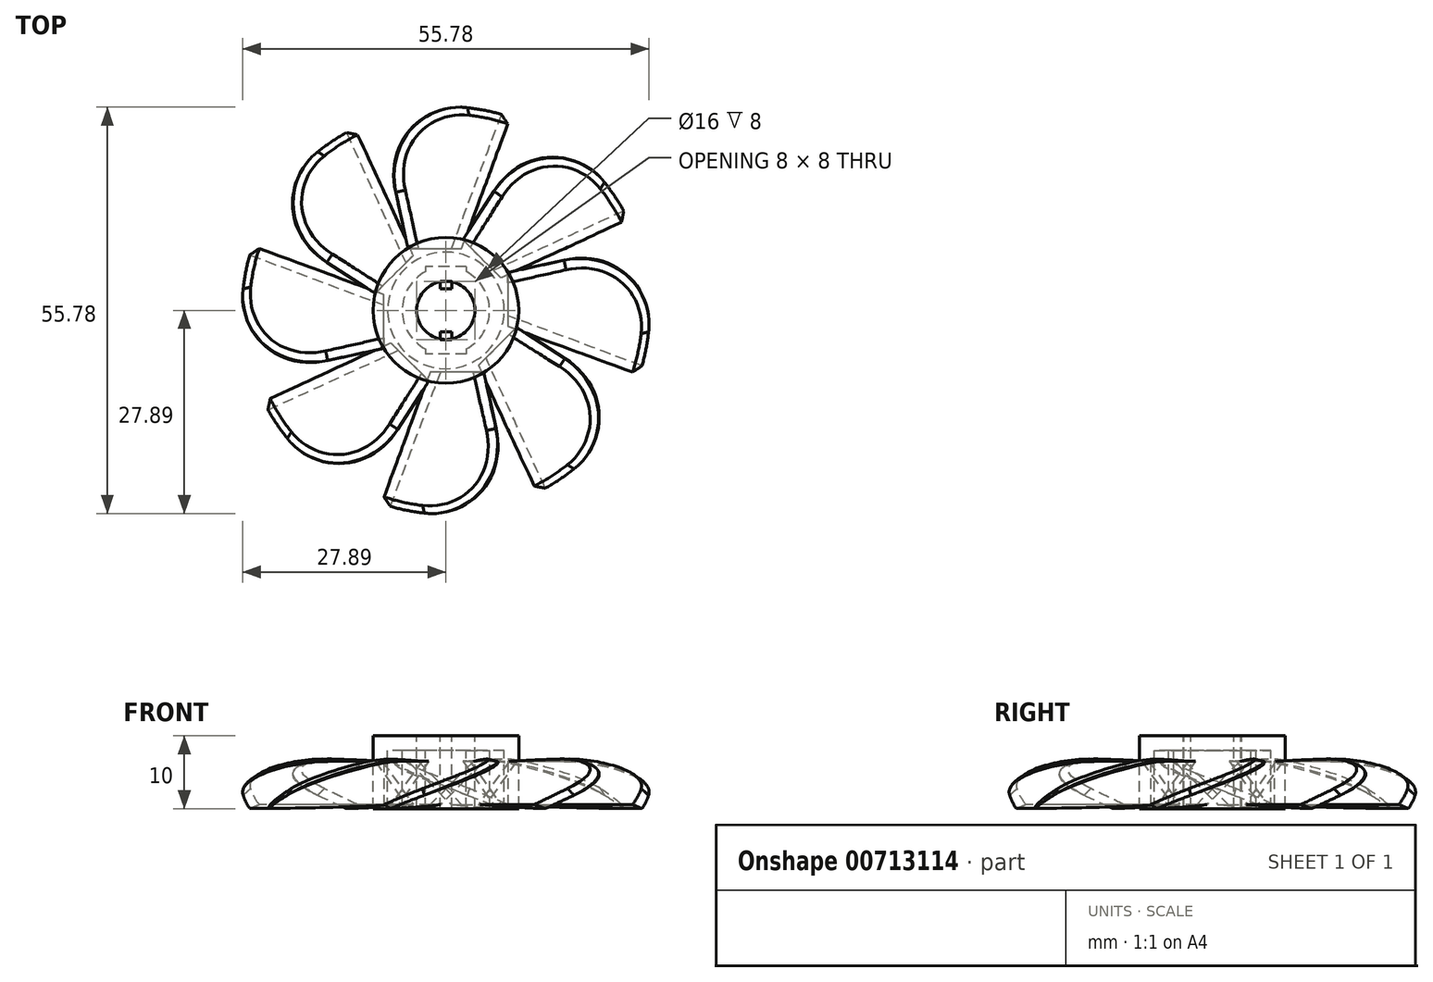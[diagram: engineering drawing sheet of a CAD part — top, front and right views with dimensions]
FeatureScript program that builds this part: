
annotation { "Feature Type Name" : "Feature", "Feature Type Description" : "" }
export const myFeature = defineFeature(function(context is Context, id is Id, definition is map)
    precondition{}
    {
        {
            var Q0;
            Q0=qCreatedBy(makeId("Top.planeOp"),FACE);
            var sketch = newSketch(context, id + "F0", { "sketchPlane" : qUnion([Q0])});
            skCircle(sketch, "E0", {"center": v(0, 0) * mm, "radius": 4 * mm});
            skCircle(sketch, "E1", {"center": v(0, 0) * mm, "radius": 10 * mm});
            skLineSegment(sketch, "E2.bottom", {"start": v(0.8, 4) * mm, "end": v(-0.8, 4) * mm});
            skLineSegment(sketch, "E2.top", {"start": v(0.8, -4) * mm, "end": v(-0.8, -4) * mm});
            skLineSegment(sketch, "E2.left", {"start": v(0.8, 4) * mm, "end": v(0.8, -4) * mm});
            skLineSegment(sketch, "E2.right", {"start": v(-0.8, 4) * mm, "end": v(-0.8, -4) * mm});
            skCircle(sketch, "E3", {"center": v(0, 0) * mm, "radius": 28 * mm});
            skCircle(sketch, "E4", {"center": v(0, 0) * mm, "radius": 44.62 * mm});
            skLineSegment(sketch, "E5.bottom", {"start": v(-0.8, 4) * mm, "end": v(0.8, 4) * mm});
            skLineSegment(sketch, "E5.top", {"start": v(-0.8, 2.95) * mm, "end": v(0.8, 2.95) * mm});
            skLineSegment(sketch, "E5.left", {"start": v(-0.8, 4) * mm, "end": v(-0.8, 2.95) * mm});
            skLineSegment(sketch, "E5.right", {"start": v(0.8, 4) * mm, "end": v(0.8, 2.95) * mm});
            skLineSegment(sketch, "E6.bottom", {"start": v(-0.8, -4) * mm, "end": v(0.8, -4) * mm});
            skLineSegment(sketch, "E6.top", {"start": v(-0.8, -2.95) * mm, "end": v(0.8, -2.95) * mm});
            skLineSegment(sketch, "E6.left", {"start": v(-0.8, -4) * mm, "end": v(-0.8, -2.95) * mm});
            skLineSegment(sketch, "E6.right", {"start": v(0.8, -4) * mm, "end": v(0.8, -2.95) * mm});
            skSolve(sketch);
        }
        {
            var Q0;
            Q0=makeQuery(id+"F0.imprint","IMPRINT",FACE,{"disambiguationData":[TD([[makeQuery(id+"F0.imprint","IMPRINT",EDGE,{"derivedFrom":sQuery(id+"F0.wireOp",EDGE,"E1")}),1.0]])]});
            var Q1;
            {var subQ0=sQuery(id+"F0.wireOp",EDGE,"E5.top");Q1=makeQuery(id+"F0.imprint","IMPRINT",FACE,{"disambiguationData":[TD([[makeQuery(id+"F0.imprint","IMPRINT",EDGE,{"derivedFrom":subQ0}),1.0]])]});}
            var Q2;
            {var subQ1=sQuery(id+"F0.wireOp",EDGE,"E6.top");Q2=makeQuery(id+"F0.imprint","IMPRINT",FACE,{"disambiguationData":[TD([[makeQuery(id+"F0.imprint","IMPRINT",EDGE,{"derivedFrom":subQ1}),-1.0]])]});}
            var Q3;
            {var subQ0=sQuery(id+"F0.wireOp",EDGE,"E6.bottom");var subQ1=sQuery(id+"F0.wireOp",EDGE,"E0");var subQ2=makeQuery(id+"F0.imprint","INTERSECT",VERTEX,{"derivedFrom":[subQ1,subQ0]});Q3=makeQuery(id+"F0.imprint","IMPRINT",FACE,{"disambiguationData":[TD([[makeQuery(id+"F0.imprint","IMPRINT",EDGE,{"disambiguationData":[TD([[subQ2,-1.0]])],"derivedFrom":subQ1}),-1.0]])]});}
            var Q4;
            {var subQ0=sQuery(id+"F0.wireOp",EDGE,"E6.left");var subQ1=sQuery(id+"F0.wireOp",EDGE,"E0");var subQ2=makeQuery(id+"F0.imprint","INTERSECT",VERTEX,{"derivedFrom":[subQ1,subQ0]});Q4=makeQuery(id+"F0.imprint","IMPRINT",FACE,{"disambiguationData":[TD([[makeQuery(id+"F0.imprint","IMPRINT",EDGE,{"disambiguationData":[TD([[subQ2,-1.0]])],"derivedFrom":subQ1}),-1.0]])]});}
            var Q5;
            {var subQ0=sQuery(id+"F0.wireOp",EDGE,"E5.bottom");var subQ1=sQuery(id+"F0.wireOp",EDGE,"E0");var subQ2=makeQuery(id+"F0.imprint","INTERSECT",VERTEX,{"derivedFrom":[subQ1,subQ0]});Q5=makeQuery(id+"F0.imprint","IMPRINT",FACE,{"disambiguationData":[TD([[makeQuery(id+"F0.imprint","IMPRINT",EDGE,{"disambiguationData":[TD([[subQ2,-1.0]])],"derivedFrom":subQ1}),-1.0]])]});}
            var Q6;
            {var subQ0=sQuery(id+"F0.wireOp",EDGE,"E5.bottom");var subQ1=sQuery(id+"F0.wireOp",EDGE,"E0");var subQ2=makeQuery(id+"F0.imprint","INTERSECT",VERTEX,{"derivedFrom":[subQ1,subQ0]});Q6=makeQuery(id+"F0.imprint","IMPRINT",FACE,{"disambiguationData":[TD([[makeQuery(id+"F0.imprint","IMPRINT",EDGE,{"disambiguationData":[TD([[subQ2,1.0]])],"derivedFrom":subQ1}),-1.0]])]});}
            extrude(context, id + "F1", {"entities" : qUnion([Q0, Q1, Q2, Q3, Q4, Q5, Q6]), "oppositeDirection" : true, "depth" : 10 * mm, "offsetDistance" : 25 * mm});
        }
        {
            var Q0;
            Q0=makeQuery(id+"F1.opExtrude","CAP_FACE",FACE,{"disambiguationData":[OSD([sQuery(id+"F0.wireOp",EDGE,"E1")])],"isStart":false});
            shell(context, id + "F2", {"entities" : qUnion([Q0]), "thickness" : 2 * mm});
        }
        {
            var Q0;
            Q0=qCreatedBy(makeId("Right.planeOp"),FACE);
            var sketch = newSketch(context, id + "F3", { "sketchPlane" : qUnion([Q0])});
            skLineSegment(sketch, "E7", {"start": v(0, 0) * mm, "end": v(0, -13) * mm});
            skSolve(sketch);
        }
        {
            var Q0;
            Q0=qCreatedBy(makeId("Front.planeOp"),FACE);
            cPlane(context, id + "F4", {"entities" : qUnion([Q0]), "cplaneType" : CPlaneType.OFFSET, "offset" : 8.5 * mm, "width" : 150 * mm, "height" : 150 * mm});
        }
        {
            var Q0;
            Q0=qCreatedBy(id+"F4.planeOp",FACE);
            var sketch = newSketch(context, id + "F5", { "sketchPlane" : qUnion([Q0])});
            skLineSegment(sketch, "E8", {"start": v(0, 0) * mm, "end": v(0, -6.5) * mm});
            skLineSegment(sketch, "E9.bottom", {"start": v(5.21, -3.5) * mm, "end": v(4.5, -2.79) * mm});
            skLineSegment(sketch, "E9.top", {"start": v(-1.5, -10.21) * mm, "end": v(-2.21, -9.5) * mm});
            skLineSegment(sketch, "E9.left", {"start": v(5.21, -3.5) * mm, "end": v(-1.5, -10.21) * mm});
            skLineSegment(sketch, "E9.right", {"start": v(4.5, -2.79) * mm, "end": v(-2.21, -9.5) * mm});
            skPoint(sketch, "E9.middle", {"position": v(1.5, -6.5) * mm});
            skLineSegment(sketch, "E10", {"start": v(0, -6.5) * mm, "end": v(1.5, -6.5) * mm, "construction": true});
            skSolve(sketch);
        }
        {
            var Q0;
            {var subQ0=sQuery(id+"F5.wireOp",EDGE,"E9.bottom");Q0=makeQuery(id+"F5.imprint","IMPRINT",FACE,{"disambiguationData":[TD([[makeQuery(id+"F5.imprint","IMPRINT",EDGE,{"derivedFrom":subQ0}),1.0]])]});}
            cPlane(context, id + "F6", {"entities" : qUnion([Q0]), "cplaneType" : CPlaneType.OFFSET, "offset" : 20 * mm, "width" : 150 * mm, "height" : 150 * mm});
        }
        {
            var Q0;
            Q0=qCreatedBy(id+"F6.planeOp",FACE);
            var sketch = newSketch(context, id + "F7", { "sketchPlane" : qUnion([Q0])});
            skLineSegment(sketch, "E11.bottom", {"start": v(9.57, -3.55) * mm, "end": v(9.23, -2.6) * mm});
            skLineSegment(sketch, "E11.top", {"start": v(-9.23, -10.4) * mm, "end": v(-9.57, -9.45) * mm});
            skLineSegment(sketch, "E11.left", {"start": v(9.57, -3.55) * mm, "end": v(-9.23, -10.4) * mm});
            skLineSegment(sketch, "E11.right", {"start": v(9.23, -2.6) * mm, "end": v(-9.57, -9.45) * mm});
            skPoint(sketch, "E11.middle", {"position": v(0, -6.5) * mm});
            skSolve(sketch);
        }
        {
            var Q0;
            {var subQ0=sQuery(id+"F5.wireOp",EDGE,"E9.bottom");Q0=makeQuery(id+"F5.imprint","IMPRINT",FACE,{"disambiguationData":[TD([[makeQuery(id+"F5.imprint","IMPRINT",EDGE,{"derivedFrom":subQ0}),1.0]])]});}
            var Q1;
            Q1=makeQuery(id+"F7.imprint","IMPRINT",FACE,{"disambiguationData":[TD([[makeQuery(id+"F7.imprint","IMPRINT",EDGE,{"derivedFrom":sQuery(id+"F7.wireOp",EDGE,"E11.bottom")}),1.0]])]});
            loft(context, id + "F8", {"sheetProfilesArray" : [{ "sheetProfileEntities" : qUnion([Q0]) }, { "sheetProfileEntities" : qUnion([Q1]) }]});
        }
        {
            var Q0;
            Q0=makeQuery(id+"F8.opLoft","SWEPT_BODY",BODY,{"disambiguationData":[OSD([makeQuery(id+"F5.imprint","IMPRINT",FACE,{"disambiguationData":[TD([[makeQuery(id+"F5.imprint","IMPRINT",EDGE,{"derivedFrom":sQuery(id+"F5.wireOp",EDGE,"E9.bottom")}),1.0]])]}),makeQuery(id+"F7.imprint","IMPRINT",FACE,{"disambiguationData":[TD([[makeQuery(id+"F7.imprint","IMPRINT",EDGE,{"derivedFrom":sQuery(id+"F7.wireOp",EDGE,"E11.bottom")}),1.0]])]})])]});
            var Q1;
            Q1=sQuery(id+"F3.wireOp",EDGE,"E7");
            circularPattern(context, id + "F9", {"entities" : qUnion([Q0]), "axis" : qUnion([Q1]), "angle" : 360 * degree, "instanceCount" : 8, "equalSpace" : true});
        }
        {
            var Q0;
            Q0=makeQuery(id+"F0.imprint","IMPRINT",FACE,{"disambiguationData":[TD([[makeQuery(id+"F0.imprint","IMPRINT",EDGE,{"derivedFrom":sQuery(id+"F0.wireOp",EDGE,"E3")}),-1.0]])]});
            extrude(context, id + "F10", {"entities" : qUnion([Q0]), "operationType" : NewBodyOperationType.REMOVE, "oppositeDirection" : true, "depth" : 25 * mm, "offsetDistance" : 25 * mm});
        }
        {
            var Q0;
            Q0=makeQuery(id+"F10.boolean.opBoolean","INTERSECT",EDGE,{"derivedFrom":[makeQuery(id+"F8.opLoft","SWEPT_FACE",FACE,{"disambiguationData":[OSD([sQuery(id+"F5.wireOp",EDGE,"E9.bottom"),sQuery(id+"F5.wireOp",EDGE,"E9.left"),sQuery(id+"F5.wireOp",EDGE,"E9.right"),sQuery(id+"F7.wireOp",EDGE,"E11.bottom"),sQuery(id+"F7.wireOp",EDGE,"E11.left"),sQuery(id+"F7.wireOp",EDGE,"E11.right")])]}),makeQuery(id+"F10.opExtrude","SWEPT_FACE",FACE,{"disambiguationData":[OSD([sQuery(id+"F0.wireOp",EDGE,"E3")])]})]});
            var Q1;
            Q1=makeQuery(id+"F10.boolean.opBoolean","INTERSECT",EDGE,{"derivedFrom":[makeQuery(id+"F9.opPattern","COPY",FACE,{"derivedFrom":makeQuery(id+"F8.opLoft","SWEPT_FACE",FACE,{"disambiguationData":[OSD([sQuery(id+"F5.wireOp",EDGE,"E9.bottom"),sQuery(id+"F5.wireOp",EDGE,"E9.left"),sQuery(id+"F5.wireOp",EDGE,"E9.right"),sQuery(id+"F7.wireOp",EDGE,"E11.bottom"),sQuery(id+"F7.wireOp",EDGE,"E11.left"),sQuery(id+"F7.wireOp",EDGE,"E11.right")])]}),"instanceName":"6"}),makeQuery(id+"F10.opExtrude","SWEPT_FACE",FACE,{"disambiguationData":[OSD([sQuery(id+"F0.wireOp",EDGE,"E3")])]})]});
            var Q2;
            Q2=makeQuery(id+"F10.boolean.opBoolean","INTERSECT",EDGE,{"derivedFrom":[makeQuery(id+"F9.opPattern","COPY",FACE,{"derivedFrom":makeQuery(id+"F8.opLoft","SWEPT_FACE",FACE,{"disambiguationData":[OSD([sQuery(id+"F5.wireOp",EDGE,"E9.bottom"),sQuery(id+"F5.wireOp",EDGE,"E9.left"),sQuery(id+"F5.wireOp",EDGE,"E9.right"),sQuery(id+"F7.wireOp",EDGE,"E11.bottom"),sQuery(id+"F7.wireOp",EDGE,"E11.left"),sQuery(id+"F7.wireOp",EDGE,"E11.right")])]}),"instanceName":"5"}),makeQuery(id+"F10.opExtrude","SWEPT_FACE",FACE,{"disambiguationData":[OSD([sQuery(id+"F0.wireOp",EDGE,"E3")])]})]});
            var Q3;
            Q3=makeQuery(id+"F10.boolean.opBoolean","INTERSECT",EDGE,{"derivedFrom":[makeQuery(id+"F9.opPattern","COPY",FACE,{"derivedFrom":makeQuery(id+"F8.opLoft","SWEPT_FACE",FACE,{"disambiguationData":[OSD([sQuery(id+"F5.wireOp",EDGE,"E9.bottom"),sQuery(id+"F5.wireOp",EDGE,"E9.left"),sQuery(id+"F5.wireOp",EDGE,"E9.right"),sQuery(id+"F7.wireOp",EDGE,"E11.bottom"),sQuery(id+"F7.wireOp",EDGE,"E11.left"),sQuery(id+"F7.wireOp",EDGE,"E11.right")])]}),"instanceName":"4"}),makeQuery(id+"F10.opExtrude","SWEPT_FACE",FACE,{"disambiguationData":[OSD([sQuery(id+"F0.wireOp",EDGE,"E3")])]})]});
            var Q4;
            Q4=makeQuery(id+"F10.boolean.opBoolean","INTERSECT",EDGE,{"derivedFrom":[makeQuery(id+"F9.opPattern","COPY",FACE,{"derivedFrom":makeQuery(id+"F8.opLoft","SWEPT_FACE",FACE,{"disambiguationData":[OSD([sQuery(id+"F5.wireOp",EDGE,"E9.bottom"),sQuery(id+"F5.wireOp",EDGE,"E9.left"),sQuery(id+"F5.wireOp",EDGE,"E9.right"),sQuery(id+"F7.wireOp",EDGE,"E11.bottom"),sQuery(id+"F7.wireOp",EDGE,"E11.left"),sQuery(id+"F7.wireOp",EDGE,"E11.right")])]}),"instanceName":"3"}),makeQuery(id+"F10.opExtrude","SWEPT_FACE",FACE,{"disambiguationData":[OSD([sQuery(id+"F0.wireOp",EDGE,"E3")])]})]});
            var Q5;
            Q5=makeQuery(id+"F10.boolean.opBoolean","INTERSECT",EDGE,{"derivedFrom":[makeQuery(id+"F9.opPattern","COPY",FACE,{"derivedFrom":makeQuery(id+"F8.opLoft","SWEPT_FACE",FACE,{"disambiguationData":[OSD([sQuery(id+"F5.wireOp",EDGE,"E9.bottom"),sQuery(id+"F5.wireOp",EDGE,"E9.left"),sQuery(id+"F5.wireOp",EDGE,"E9.right"),sQuery(id+"F7.wireOp",EDGE,"E11.bottom"),sQuery(id+"F7.wireOp",EDGE,"E11.left"),sQuery(id+"F7.wireOp",EDGE,"E11.right")])]}),"instanceName":"2"}),makeQuery(id+"F10.opExtrude","SWEPT_FACE",FACE,{"disambiguationData":[OSD([sQuery(id+"F0.wireOp",EDGE,"E3")])]})]});
            var Q6;
            Q6=makeQuery(id+"F10.boolean.opBoolean","INTERSECT",EDGE,{"derivedFrom":[makeQuery(id+"F9.opPattern","COPY",FACE,{"derivedFrom":makeQuery(id+"F8.opLoft","SWEPT_FACE",FACE,{"disambiguationData":[OSD([sQuery(id+"F5.wireOp",EDGE,"E9.bottom"),sQuery(id+"F5.wireOp",EDGE,"E9.left"),sQuery(id+"F5.wireOp",EDGE,"E9.right"),sQuery(id+"F7.wireOp",EDGE,"E11.bottom"),sQuery(id+"F7.wireOp",EDGE,"E11.left"),sQuery(id+"F7.wireOp",EDGE,"E11.right")])]}),"instanceName":"1"}),makeQuery(id+"F10.opExtrude","SWEPT_FACE",FACE,{"disambiguationData":[OSD([sQuery(id+"F0.wireOp",EDGE,"E3")])]})]});
            var Q7;
            Q7=makeQuery(id+"F10.boolean.opBoolean","INTERSECT",EDGE,{"derivedFrom":[makeQuery(id+"F9.opPattern","COPY",FACE,{"derivedFrom":makeQuery(id+"F8.opLoft","SWEPT_FACE",FACE,{"disambiguationData":[OSD([sQuery(id+"F5.wireOp",EDGE,"E9.bottom"),sQuery(id+"F5.wireOp",EDGE,"E9.left"),sQuery(id+"F5.wireOp",EDGE,"E9.right"),sQuery(id+"F7.wireOp",EDGE,"E11.bottom"),sQuery(id+"F7.wireOp",EDGE,"E11.left"),sQuery(id+"F7.wireOp",EDGE,"E11.right")])]}),"instanceName":"7"}),makeQuery(id+"F10.opExtrude","SWEPT_FACE",FACE,{"disambiguationData":[OSD([sQuery(id+"F0.wireOp",EDGE,"E3")])]})]});
            fillet(context, id + "F11", {"entities" : qUnion([Q0, Q1, Q2, Q3, Q4, Q5, Q6, Q7]), "radius" : 10 * mm, "tangentPropagation" : true, "allowEdgeOverflow" : false});
        }
        {
            var Q0;
            Q0=makeQuery(id+"F8.opLoft","SWEPT_EDGE",EDGE,{"disambiguationData":[OSD([sQuery(id+"F5.wireOp",EDGE,"E9.top"),sQuery(id+"F5.wireOp",EDGE,"E9.left"),sQuery(id+"F7.wireOp",EDGE,"E11.top"),sQuery(id+"F7.wireOp",EDGE,"E11.left")])]});
            var Q1;
            Q1=makeQuery(id+"F9.opPattern","COPY",EDGE,{"derivedFrom":makeQuery(id+"F8.opLoft","SWEPT_EDGE",EDGE,{"disambiguationData":[OSD([sQuery(id+"F5.wireOp",EDGE,"E9.top"),sQuery(id+"F5.wireOp",EDGE,"E9.left"),sQuery(id+"F7.wireOp",EDGE,"E11.top"),sQuery(id+"F7.wireOp",EDGE,"E11.left")])]}),"instanceName":"7"});
            var Q2;
            Q2=makeQuery(id+"F9.opPattern","COPY",EDGE,{"derivedFrom":makeQuery(id+"F8.opLoft","SWEPT_EDGE",EDGE,{"disambiguationData":[OSD([sQuery(id+"F5.wireOp",EDGE,"E9.top"),sQuery(id+"F5.wireOp",EDGE,"E9.left"),sQuery(id+"F7.wireOp",EDGE,"E11.top"),sQuery(id+"F7.wireOp",EDGE,"E11.left")])]}),"instanceName":"6"});
            var Q3;
            Q3=makeQuery(id+"F9.opPattern","COPY",EDGE,{"derivedFrom":makeQuery(id+"F8.opLoft","SWEPT_EDGE",EDGE,{"disambiguationData":[OSD([sQuery(id+"F5.wireOp",EDGE,"E9.top"),sQuery(id+"F5.wireOp",EDGE,"E9.left"),sQuery(id+"F7.wireOp",EDGE,"E11.top"),sQuery(id+"F7.wireOp",EDGE,"E11.left")])]}),"instanceName":"5"});
            var Q4;
            Q4=makeQuery(id+"F9.opPattern","COPY",EDGE,{"derivedFrom":makeQuery(id+"F8.opLoft","SWEPT_EDGE",EDGE,{"disambiguationData":[OSD([sQuery(id+"F5.wireOp",EDGE,"E9.top"),sQuery(id+"F5.wireOp",EDGE,"E9.left"),sQuery(id+"F7.wireOp",EDGE,"E11.top"),sQuery(id+"F7.wireOp",EDGE,"E11.left")])]}),"instanceName":"4"});
            var Q5;
            Q5=makeQuery(id+"F9.opPattern","COPY",EDGE,{"derivedFrom":makeQuery(id+"F8.opLoft","SWEPT_EDGE",EDGE,{"disambiguationData":[OSD([sQuery(id+"F5.wireOp",EDGE,"E9.top"),sQuery(id+"F5.wireOp",EDGE,"E9.left"),sQuery(id+"F7.wireOp",EDGE,"E11.top"),sQuery(id+"F7.wireOp",EDGE,"E11.left")])]}),"instanceName":"3"});
            var Q6;
            Q6=makeQuery(id+"F9.opPattern","COPY",EDGE,{"derivedFrom":makeQuery(id+"F8.opLoft","SWEPT_EDGE",EDGE,{"disambiguationData":[OSD([sQuery(id+"F5.wireOp",EDGE,"E9.top"),sQuery(id+"F5.wireOp",EDGE,"E9.left"),sQuery(id+"F7.wireOp",EDGE,"E11.top"),sQuery(id+"F7.wireOp",EDGE,"E11.left")])]}),"instanceName":"2"});
            var Q7;
            Q7=makeQuery(id+"F9.opPattern","COPY",EDGE,{"derivedFrom":makeQuery(id+"F8.opLoft","SWEPT_EDGE",EDGE,{"disambiguationData":[OSD([sQuery(id+"F5.wireOp",EDGE,"E9.top"),sQuery(id+"F5.wireOp",EDGE,"E9.left"),sQuery(id+"F7.wireOp",EDGE,"E11.top"),sQuery(id+"F7.wireOp",EDGE,"E11.left")])]}),"instanceName":"1"});
            var Q8;
            Q8=makeQuery(id+"F9.opPattern","COPY",EDGE,{"derivedFrom":makeQuery(id+"F8.opLoft","SWEPT_EDGE",EDGE,{"disambiguationData":[OSD([sQuery(id+"F5.wireOp",EDGE,"E9.bottom"),sQuery(id+"F5.wireOp",EDGE,"E9.right"),sQuery(id+"F7.wireOp",EDGE,"E11.bottom"),sQuery(id+"F7.wireOp",EDGE,"E11.right")])]}),"instanceName":"1"});
            var Q9;
            {var subQ0=sQuery(id+"F7.wireOp",EDGE,"E11.right");var subQ1=sQuery(id+"F7.wireOp",EDGE,"E11.bottom");var subQ2=sQuery(id+"F5.wireOp",EDGE,"E9.right");var subQ3=sQuery(id+"F5.wireOp",EDGE,"E9.bottom");Q9=makeQuery(id+"F11.opFillet","BLEND_EDGE",EDGE,{"blendedFrom":[makeQuery(id+"F10.boolean.opBoolean","INTERSECT",EDGE,{"derivedFrom":[makeQuery(id+"F8.opLoft","SWEPT_FACE",FACE,{"disambiguationData":[OSD([subQ3,sQuery(id+"F5.wireOp",EDGE,"E9.left"),subQ2,subQ1,sQuery(id+"F7.wireOp",EDGE,"E11.left"),subQ0])]}),makeQuery(id+"F10.opExtrude","SWEPT_FACE",FACE,{"disambiguationData":[OSD([sQuery(id+"F0.wireOp",EDGE,"E3")])]})]}),makeQuery(id+"F8.opLoft","SWEPT_FACE",FACE,{"disambiguationData":[OSD([subQ3,sQuery(id+"F5.wireOp",EDGE,"E9.top"),subQ2,subQ1,sQuery(id+"F7.wireOp",EDGE,"E11.top"),subQ0])]})],"blendedInto":[makeQuery(id+"F8.opLoft","SWEPT_FACE",FACE,{"disambiguationData":[OSD([subQ3,sQuery(id+"F5.wireOp",EDGE,"E9.top"),subQ2,subQ1,sQuery(id+"F7.wireOp",EDGE,"E11.top"),subQ0])]})]});}
            var Q10;
            {var subQ0=sQuery(id+"F7.wireOp",EDGE,"E11.right");var subQ1=sQuery(id+"F7.wireOp",EDGE,"E11.bottom");var subQ2=sQuery(id+"F5.wireOp",EDGE,"E9.right");var subQ3=sQuery(id+"F5.wireOp",EDGE,"E9.bottom");Q10=makeQuery(id+"F11.opFillet","BLEND_EDGE",EDGE,{"blendedFrom":[makeQuery(id+"F10.boolean.opBoolean","INTERSECT",EDGE,{"derivedFrom":[makeQuery(id+"F9.opPattern","COPY",FACE,{"derivedFrom":makeQuery(id+"F8.opLoft","SWEPT_FACE",FACE,{"disambiguationData":[OSD([subQ3,sQuery(id+"F5.wireOp",EDGE,"E9.left"),subQ2,subQ1,sQuery(id+"F7.wireOp",EDGE,"E11.left"),subQ0])]}),"instanceName":"7"}),makeQuery(id+"F10.opExtrude","SWEPT_FACE",FACE,{"disambiguationData":[OSD([sQuery(id+"F0.wireOp",EDGE,"E3")])]})]}),makeQuery(id+"F9.opPattern","COPY",FACE,{"derivedFrom":makeQuery(id+"F8.opLoft","SWEPT_FACE",FACE,{"disambiguationData":[OSD([subQ3,sQuery(id+"F5.wireOp",EDGE,"E9.top"),subQ2,subQ1,sQuery(id+"F7.wireOp",EDGE,"E11.top"),subQ0])]}),"instanceName":"7"})],"blendedInto":[makeQuery(id+"F9.opPattern","COPY",FACE,{"derivedFrom":makeQuery(id+"F8.opLoft","SWEPT_FACE",FACE,{"disambiguationData":[OSD([subQ3,sQuery(id+"F5.wireOp",EDGE,"E9.top"),subQ2,subQ1,sQuery(id+"F7.wireOp",EDGE,"E11.top"),subQ0])]}),"instanceName":"7"})]});}
            var Q11;
            {var subQ0=sQuery(id+"F7.wireOp",EDGE,"E11.right");var subQ1=sQuery(id+"F7.wireOp",EDGE,"E11.bottom");var subQ2=sQuery(id+"F5.wireOp",EDGE,"E9.right");var subQ3=sQuery(id+"F5.wireOp",EDGE,"E9.bottom");Q11=makeQuery(id+"F11.opFillet","BLEND_EDGE",EDGE,{"blendedFrom":[makeQuery(id+"F10.boolean.opBoolean","INTERSECT",EDGE,{"derivedFrom":[makeQuery(id+"F9.opPattern","COPY",FACE,{"derivedFrom":makeQuery(id+"F8.opLoft","SWEPT_FACE",FACE,{"disambiguationData":[OSD([subQ3,sQuery(id+"F5.wireOp",EDGE,"E9.left"),subQ2,subQ1,sQuery(id+"F7.wireOp",EDGE,"E11.left"),subQ0])]}),"instanceName":"6"}),makeQuery(id+"F10.opExtrude","SWEPT_FACE",FACE,{"disambiguationData":[OSD([sQuery(id+"F0.wireOp",EDGE,"E3")])]})]}),makeQuery(id+"F9.opPattern","COPY",FACE,{"derivedFrom":makeQuery(id+"F8.opLoft","SWEPT_FACE",FACE,{"disambiguationData":[OSD([subQ3,sQuery(id+"F5.wireOp",EDGE,"E9.top"),subQ2,subQ1,sQuery(id+"F7.wireOp",EDGE,"E11.top"),subQ0])]}),"instanceName":"6"})],"blendedInto":[makeQuery(id+"F9.opPattern","COPY",FACE,{"derivedFrom":makeQuery(id+"F8.opLoft","SWEPT_FACE",FACE,{"disambiguationData":[OSD([subQ3,sQuery(id+"F5.wireOp",EDGE,"E9.top"),subQ2,subQ1,sQuery(id+"F7.wireOp",EDGE,"E11.top"),subQ0])]}),"instanceName":"6"})]});}
            var Q12;
            {var subQ0=sQuery(id+"F7.wireOp",EDGE,"E11.right");var subQ1=sQuery(id+"F7.wireOp",EDGE,"E11.bottom");var subQ2=sQuery(id+"F5.wireOp",EDGE,"E9.right");var subQ3=sQuery(id+"F5.wireOp",EDGE,"E9.bottom");Q12=makeQuery(id+"F11.opFillet","BLEND_EDGE",EDGE,{"blendedFrom":[makeQuery(id+"F10.boolean.opBoolean","INTERSECT",EDGE,{"derivedFrom":[makeQuery(id+"F9.opPattern","COPY",FACE,{"derivedFrom":makeQuery(id+"F8.opLoft","SWEPT_FACE",FACE,{"disambiguationData":[OSD([subQ3,sQuery(id+"F5.wireOp",EDGE,"E9.left"),subQ2,subQ1,sQuery(id+"F7.wireOp",EDGE,"E11.left"),subQ0])]}),"instanceName":"5"}),makeQuery(id+"F10.opExtrude","SWEPT_FACE",FACE,{"disambiguationData":[OSD([sQuery(id+"F0.wireOp",EDGE,"E3")])]})]}),makeQuery(id+"F9.opPattern","COPY",FACE,{"derivedFrom":makeQuery(id+"F8.opLoft","SWEPT_FACE",FACE,{"disambiguationData":[OSD([subQ3,sQuery(id+"F5.wireOp",EDGE,"E9.top"),subQ2,subQ1,sQuery(id+"F7.wireOp",EDGE,"E11.top"),subQ0])]}),"instanceName":"5"})],"blendedInto":[makeQuery(id+"F9.opPattern","COPY",FACE,{"derivedFrom":makeQuery(id+"F8.opLoft","SWEPT_FACE",FACE,{"disambiguationData":[OSD([subQ3,sQuery(id+"F5.wireOp",EDGE,"E9.top"),subQ2,subQ1,sQuery(id+"F7.wireOp",EDGE,"E11.top"),subQ0])]}),"instanceName":"5"})]});}
            var Q13;
            {var subQ0=sQuery(id+"F7.wireOp",EDGE,"E11.right");var subQ1=sQuery(id+"F7.wireOp",EDGE,"E11.bottom");var subQ2=sQuery(id+"F5.wireOp",EDGE,"E9.right");var subQ3=sQuery(id+"F5.wireOp",EDGE,"E9.bottom");Q13=makeQuery(id+"F11.opFillet","BLEND_EDGE",EDGE,{"blendedFrom":[makeQuery(id+"F10.boolean.opBoolean","INTERSECT",EDGE,{"derivedFrom":[makeQuery(id+"F9.opPattern","COPY",FACE,{"derivedFrom":makeQuery(id+"F8.opLoft","SWEPT_FACE",FACE,{"disambiguationData":[OSD([subQ3,sQuery(id+"F5.wireOp",EDGE,"E9.left"),subQ2,subQ1,sQuery(id+"F7.wireOp",EDGE,"E11.left"),subQ0])]}),"instanceName":"4"}),makeQuery(id+"F10.opExtrude","SWEPT_FACE",FACE,{"disambiguationData":[OSD([sQuery(id+"F0.wireOp",EDGE,"E3")])]})]}),makeQuery(id+"F9.opPattern","COPY",FACE,{"derivedFrom":makeQuery(id+"F8.opLoft","SWEPT_FACE",FACE,{"disambiguationData":[OSD([subQ3,sQuery(id+"F5.wireOp",EDGE,"E9.top"),subQ2,subQ1,sQuery(id+"F7.wireOp",EDGE,"E11.top"),subQ0])]}),"instanceName":"4"})],"blendedInto":[makeQuery(id+"F9.opPattern","COPY",FACE,{"derivedFrom":makeQuery(id+"F8.opLoft","SWEPT_FACE",FACE,{"disambiguationData":[OSD([subQ3,sQuery(id+"F5.wireOp",EDGE,"E9.top"),subQ2,subQ1,sQuery(id+"F7.wireOp",EDGE,"E11.top"),subQ0])]}),"instanceName":"4"})]});}
            var Q14;
            {var subQ0=sQuery(id+"F7.wireOp",EDGE,"E11.right");var subQ1=sQuery(id+"F7.wireOp",EDGE,"E11.bottom");var subQ2=sQuery(id+"F5.wireOp",EDGE,"E9.right");var subQ3=sQuery(id+"F5.wireOp",EDGE,"E9.bottom");Q14=makeQuery(id+"F11.opFillet","BLEND_EDGE",EDGE,{"blendedFrom":[makeQuery(id+"F10.boolean.opBoolean","INTERSECT",EDGE,{"derivedFrom":[makeQuery(id+"F9.opPattern","COPY",FACE,{"derivedFrom":makeQuery(id+"F8.opLoft","SWEPT_FACE",FACE,{"disambiguationData":[OSD([subQ3,sQuery(id+"F5.wireOp",EDGE,"E9.left"),subQ2,subQ1,sQuery(id+"F7.wireOp",EDGE,"E11.left"),subQ0])]}),"instanceName":"3"}),makeQuery(id+"F10.opExtrude","SWEPT_FACE",FACE,{"disambiguationData":[OSD([sQuery(id+"F0.wireOp",EDGE,"E3")])]})]}),makeQuery(id+"F9.opPattern","COPY",FACE,{"derivedFrom":makeQuery(id+"F8.opLoft","SWEPT_FACE",FACE,{"disambiguationData":[OSD([subQ3,sQuery(id+"F5.wireOp",EDGE,"E9.top"),subQ2,subQ1,sQuery(id+"F7.wireOp",EDGE,"E11.top"),subQ0])]}),"instanceName":"3"})],"blendedInto":[makeQuery(id+"F9.opPattern","COPY",FACE,{"derivedFrom":makeQuery(id+"F8.opLoft","SWEPT_FACE",FACE,{"disambiguationData":[OSD([subQ3,sQuery(id+"F5.wireOp",EDGE,"E9.top"),subQ2,subQ1,sQuery(id+"F7.wireOp",EDGE,"E11.top"),subQ0])]}),"instanceName":"3"})]});}
            var Q15;
            {var subQ0=sQuery(id+"F7.wireOp",EDGE,"E11.right");var subQ1=sQuery(id+"F7.wireOp",EDGE,"E11.bottom");var subQ2=sQuery(id+"F5.wireOp",EDGE,"E9.right");var subQ3=sQuery(id+"F5.wireOp",EDGE,"E9.bottom");Q15=makeQuery(id+"F11.opFillet","BLEND_EDGE",EDGE,{"blendedFrom":[makeQuery(id+"F10.boolean.opBoolean","INTERSECT",EDGE,{"derivedFrom":[makeQuery(id+"F9.opPattern","COPY",FACE,{"derivedFrom":makeQuery(id+"F8.opLoft","SWEPT_FACE",FACE,{"disambiguationData":[OSD([subQ3,sQuery(id+"F5.wireOp",EDGE,"E9.left"),subQ2,subQ1,sQuery(id+"F7.wireOp",EDGE,"E11.left"),subQ0])]}),"instanceName":"2"}),makeQuery(id+"F10.opExtrude","SWEPT_FACE",FACE,{"disambiguationData":[OSD([sQuery(id+"F0.wireOp",EDGE,"E3")])]})]}),makeQuery(id+"F9.opPattern","COPY",FACE,{"derivedFrom":makeQuery(id+"F8.opLoft","SWEPT_FACE",FACE,{"disambiguationData":[OSD([subQ3,sQuery(id+"F5.wireOp",EDGE,"E9.top"),subQ2,subQ1,sQuery(id+"F7.wireOp",EDGE,"E11.top"),subQ0])]}),"instanceName":"2"})],"blendedInto":[makeQuery(id+"F9.opPattern","COPY",FACE,{"derivedFrom":makeQuery(id+"F8.opLoft","SWEPT_FACE",FACE,{"disambiguationData":[OSD([subQ3,sQuery(id+"F5.wireOp",EDGE,"E9.top"),subQ2,subQ1,sQuery(id+"F7.wireOp",EDGE,"E11.top"),subQ0])]}),"instanceName":"2"})]});}
            chamfer(context, id + "F12", {"entities" : qUnion([Q0, Q1, Q2, Q3, Q4, Q5, Q6, Q7, Q8, Q9, Q10, Q11, Q12, Q13, Q14, Q15]), "width" : 1 * mm, "tangentPropagation" : true});
        }
    });
